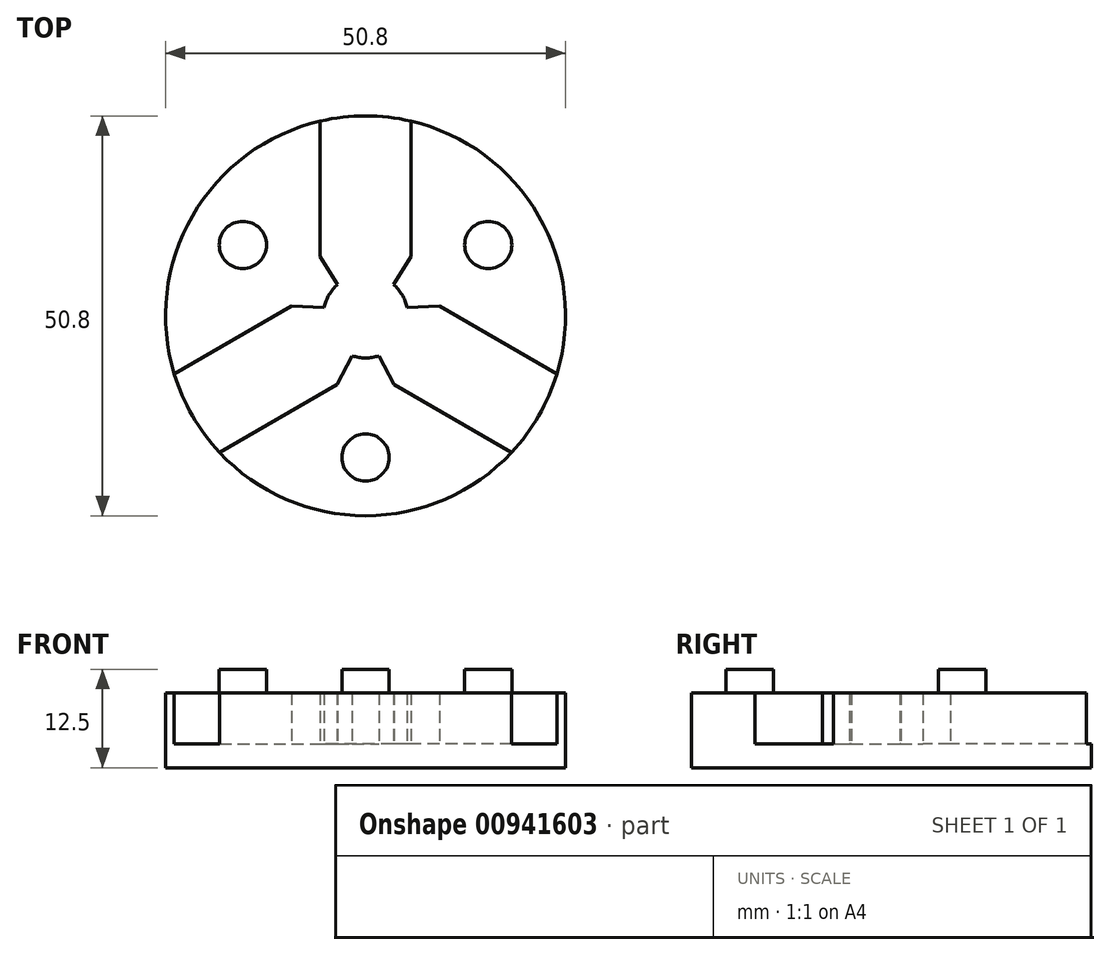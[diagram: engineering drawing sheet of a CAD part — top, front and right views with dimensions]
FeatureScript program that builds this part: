
annotation { "Feature Type Name" : "Feature", "Feature Type Description" : "" }
export const myFeature = defineFeature(function(context is Context, id is Id, definition is map)
    precondition{}
    {
        {
            var Q0;
            Q0=qCreatedBy(makeId("Top.planeOp"),FACE);
            var sketch = newSketch(context, id + "F0", { "sketchPlane" : qUnion([Q0])});
            skCircle(sketch, "E0", {"center": v(0, 0) * mm, "radius": 5.35 * mm});
            skCircle(sketch, "E1.cCircle", {"center": v(0, 0) * mm, "radius": 5.35 * mm, "construction": true});
            skLineSegment(sketch, "E2", {"start": v(0, 25.4) * mm, "end": v(5.75, 25.4) * mm});
            skLineSegment(sketch, "E3", {"start": v(5.75, 7.5) * mm, "end": v(5.75, 25.4) * mm});
            skLineSegment(sketch, "E4", {"start": v(3.55, 4) * mm, "end": v(5.75, 7.5) * mm});
            skLineSegment(sketch, "E5", {"start": v(22, -12.7) * mm, "end": v(24.87, -7.72) * mm});
            skLineSegment(sketch, "E6", {"start": v(9.37, 1.23) * mm, "end": v(24.87, -7.72) * mm});
            skLineSegment(sketch, "E7", {"start": v(5.24, 1.08) * mm, "end": v(9.37, 1.23) * mm});
            skLineSegment(sketch, "E8.MirrorCS", {"start": v(3.62, -8.73) * mm, "end": v(19.12, -17.68) * mm});
            skLineSegment(sketch, "E9.MirrorCS", {"start": v(22, -12.7) * mm, "end": v(19.12, -17.68) * mm});
            skLineSegment(sketch, "E10.MirrorCS", {"start": v(1.69, -5.08) * mm, "end": v(3.62, -8.73) * mm});
            skLineSegment(sketch, "E11.MirrorCS", {"start": v(0, 25.4) * mm, "end": v(-5.75, 25.4) * mm});
            skLineSegment(sketch, "E12.MirrorCS", {"start": v(-5.75, 7.5) * mm, "end": v(-5.75, 25.4) * mm});
            skLineSegment(sketch, "E13.MirrorCS", {"start": v(-3.55, 4) * mm, "end": v(-5.75, 7.5) * mm});
            skLineSegment(sketch, "E14.MirrorCS", {"start": v(-5.24, 1.08) * mm, "end": v(-9.37, 1.23) * mm});
            skLineSegment(sketch, "E15.MirrorCS", {"start": v(-9.37, 1.23) * mm, "end": v(-24.87, -7.72) * mm});
            skLineSegment(sketch, "E16.MirrorCS", {"start": v(-22, -12.7) * mm, "end": v(-24.87, -7.72) * mm});
            skLineSegment(sketch, "E17.MirrorCS", {"start": v(-22, -12.7) * mm, "end": v(-19.12, -17.68) * mm});
            skLineSegment(sketch, "E18.MirrorCS", {"start": v(-3.62, -8.73) * mm, "end": v(-19.12, -17.68) * mm});
            skLineSegment(sketch, "E19.MirrorCS", {"start": v(-1.69, -5.08) * mm, "end": v(-3.62, -8.73) * mm});
            skPoint(sketch, "E20", {"position": v(15.59, 9) * mm});
            skPoint(sketch, "E21.MirrorP", {"position": v(-15.59, 9) * mm});
            skPoint(sketch, "E22", {"position": v(0, -18) * mm});
            skCircle(sketch, "E23", {"center": v(0, 0) * mm, "radius": 25.4 * mm});
            skCircle(sketch, "E24", {"center": v(-15.59, 9) * mm, "radius": 3 * mm});
            skCircle(sketch, "E25", {"center": v(15.59, 9) * mm, "radius": 3 * mm});
            skCircle(sketch, "E26", {"center": v(0, -18) * mm, "radius": 3 * mm});
            skSolve(sketch);
        }
        {
            var Q0;
            {var subQ4=sQuery(id+"F0.wireOp",EDGE,"E4");Q0=makeQuery(id+"F0.imprint","IMPRINT",FACE,{"disambiguationData":[TD([[makeQuery(id+"F0.imprint","IMPRINT",EDGE,{"derivedFrom":subQ4}),-1.0]])]});}
            var Q1;
            Q1=makeQuery(id+"F0.imprint","IMPRINT",FACE,{"disambiguationData":[TD([[makeQuery(id+"F0.imprint","IMPRINT",EDGE,{"derivedFrom":sQuery(id+"F0.wireOp",EDGE,"E25")}),1.0]])]});
            var Q2;
            {var subQ7=sQuery(id+"F0.wireOp",EDGE,"E4");Q2=makeQuery(id+"F0.imprint","IMPRINT",FACE,{"disambiguationData":[TD([[makeQuery(id+"F0.imprint","IMPRINT",EDGE,{"derivedFrom":subQ7}),1.0]])]});}
            var Q3;
            {var subQ0=sQuery(id+"F0.wireOp",EDGE,"E13.MirrorCS");Q3=makeQuery(id+"F0.imprint","IMPRINT",FACE,{"disambiguationData":[TD([[makeQuery(id+"F0.imprint","IMPRINT",EDGE,{"derivedFrom":subQ0}),1.0]])]});}
            var Q4;
            Q4=makeQuery(id+"F0.imprint","IMPRINT",FACE,{"disambiguationData":[TD([[makeQuery(id+"F0.imprint","IMPRINT",EDGE,{"derivedFrom":sQuery(id+"F0.wireOp",EDGE,"E24")}),1.0]])]});
            var Q5;
            {var subQ4=sQuery(id+"F0.wireOp",EDGE,"E14.MirrorCS");Q5=makeQuery(id+"F0.imprint","IMPRINT",FACE,{"disambiguationData":[TD([[makeQuery(id+"F0.imprint","IMPRINT",EDGE,{"derivedFrom":subQ4}),1.0]])]});}
            var Q6;
            {var subQ0=sQuery(id+"F0.wireOp",EDGE,"E0");var subQ4=makeQuery(id+"F0.imprint","INTERSECT",VERTEX,{"derivedFrom":[subQ0,sQuery(id+"F0.wireOp",EDGE,"E4")]});Q6=makeQuery(id+"F0.imprint","IMPRINT",FACE,{"disambiguationData":[TD([[makeQuery(id+"F0.imprint","IMPRINT",EDGE,{"disambiguationData":[TD([[subQ4,1.0]])],"derivedFrom":subQ0}),1.0]])]});}
            var Q7;
            {var subQ5=sQuery(id+"F0.wireOp",EDGE,"E7");Q7=makeQuery(id+"F0.imprint","IMPRINT",FACE,{"disambiguationData":[TD([[makeQuery(id+"F0.imprint","IMPRINT",EDGE,{"derivedFrom":subQ5}),-1.0]])]});}
            var Q8;
            {var subQ4=sQuery(id+"F0.wireOp",EDGE,"E10.MirrorCS");Q8=makeQuery(id+"F0.imprint","IMPRINT",FACE,{"disambiguationData":[TD([[makeQuery(id+"F0.imprint","IMPRINT",EDGE,{"derivedFrom":subQ4}),-1.0]])]});}
            var Q9;
            Q9=makeQuery(id+"F0.imprint","IMPRINT",FACE,{"disambiguationData":[TD([[makeQuery(id+"F0.imprint","IMPRINT",EDGE,{"derivedFrom":sQuery(id+"F0.wireOp",EDGE,"E26")}),1.0]])]});
            extrude(context, id + "F1", {"entities" : qUnion([Q0, Q1, Q2, Q3, Q4, Q5, Q6, Q7, Q8, Q9]), "depth" : 3 * mm, "offsetDistance" : 25 * mm});
        }
        {
            var Q0;
            {var subQ0=sQuery(id+"F0.wireOp",EDGE,"E13.MirrorCS");Q0=makeQuery(id+"F0.imprint","IMPRINT",FACE,{"disambiguationData":[TD([[makeQuery(id+"F0.imprint","IMPRINT",EDGE,{"derivedFrom":subQ0}),1.0]])]});}
            var Q1;
            Q1=makeQuery(id+"F0.imprint","IMPRINT",FACE,{"disambiguationData":[TD([[makeQuery(id+"F0.imprint","IMPRINT",EDGE,{"derivedFrom":sQuery(id+"F0.wireOp",EDGE,"E24")}),1.0]])]});
            var Q2;
            Q2=makeQuery(id+"F0.imprint","IMPRINT",FACE,{"disambiguationData":[TD([[makeQuery(id+"F0.imprint","IMPRINT",EDGE,{"derivedFrom":sQuery(id+"F0.wireOp",EDGE,"E25")}),1.0]])]});
            var Q3;
            {var subQ4=sQuery(id+"F0.wireOp",EDGE,"E4");Q3=makeQuery(id+"F0.imprint","IMPRINT",FACE,{"disambiguationData":[TD([[makeQuery(id+"F0.imprint","IMPRINT",EDGE,{"derivedFrom":subQ4}),-1.0]])]});}
            var Q4;
            {var subQ4=sQuery(id+"F0.wireOp",EDGE,"E10.MirrorCS");Q4=makeQuery(id+"F0.imprint","IMPRINT",FACE,{"disambiguationData":[TD([[makeQuery(id+"F0.imprint","IMPRINT",EDGE,{"derivedFrom":subQ4}),-1.0]])]});}
            var Q5;
            Q5=makeQuery(id+"F0.imprint","IMPRINT",FACE,{"disambiguationData":[TD([[makeQuery(id+"F0.imprint","IMPRINT",EDGE,{"derivedFrom":sQuery(id+"F0.wireOp",EDGE,"E26")}),1.0]])]});
            extrude(context, id + "F2", {"entities" : qUnion([Q0, Q1, Q2, Q3, Q4, Q5]), "operationType" : NewBodyOperationType.ADD, "depth" : 9.5 * mm, "offsetDistance" : 25 * mm});
        }
        {
            var Q0;
            Q0=makeQuery(id+"F0.imprint","IMPRINT",FACE,{"disambiguationData":[TD([[makeQuery(id+"F0.imprint","IMPRINT",EDGE,{"derivedFrom":sQuery(id+"F0.wireOp",EDGE,"E24")}),1.0]])]});
            var Q1;
            Q1=makeQuery(id+"F0.imprint","IMPRINT",FACE,{"disambiguationData":[TD([[makeQuery(id+"F0.imprint","IMPRINT",EDGE,{"derivedFrom":sQuery(id+"F0.wireOp",EDGE,"E26")}),1.0]])]});
            var Q2;
            Q2=makeQuery(id+"F0.imprint","IMPRINT",FACE,{"disambiguationData":[TD([[makeQuery(id+"F0.imprint","IMPRINT",EDGE,{"derivedFrom":sQuery(id+"F0.wireOp",EDGE,"E25")}),1.0]])]});
            extrude(context, id + "F3", {"entities" : qUnion([Q0, Q1, Q2]), "operationType" : NewBodyOperationType.ADD, "depth" : 12.5 * mm, "offsetDistance" : 25 * mm});
        }
    });
